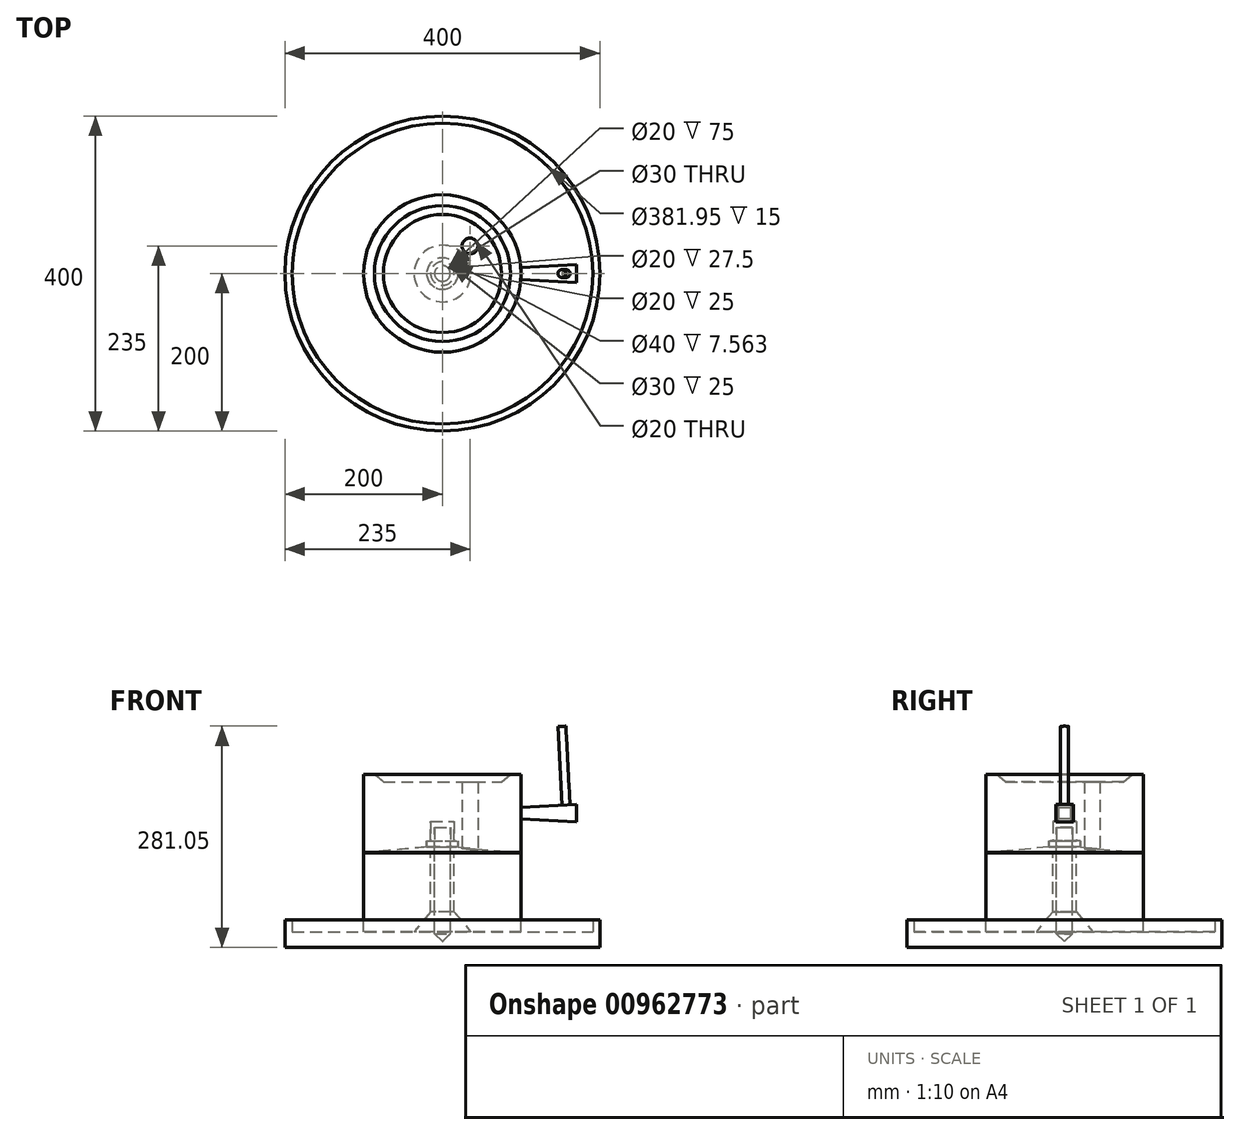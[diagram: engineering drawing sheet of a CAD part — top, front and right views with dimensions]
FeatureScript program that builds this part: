
annotation { "Feature Type Name" : "Feature", "Feature Type Description" : "" }
export const myFeature = defineFeature(function(context is Context, id is Id, definition is map)
    precondition{}
    {
        {
            var Q0;
            Q0=qCreatedBy(makeId("Top.planeOp"),FACE);
            var sketch = newSketch(context, id + "F0", { "sketchPlane" : qUnion([Q0])});
            skCircle(sketch, "E0", {"center": v(0, 0) * mm, "radius": 100 * mm});
            skCircle(sketch, "E1", {"center": v(35, 35) * mm, "radius": 10 * mm});
            skSolve(sketch);
        }
        {
            var Q0;
            Q0=qSketchRegion(id+"F0",true);
            extrude(context, id + "F1", {"entities" : qUnion([Q0]), "depth" : 100 * mm, "offsetDistance" : 25 * mm});
        }
        {
            var Q0;
            Q0=qCreatedBy(makeId("Front.planeOp"),FACE);
            var sketch = newSketch(context, id + "F2", { "sketchPlane" : qUnion([Q0])});
            skLineSegment(sketch, "E2", {"start": v(0, 40) * mm, "end": v(15, 40) * mm});
            skLineSegment(sketch, "E3", {"start": v(0, 0) * mm, "end": v(0, 40) * mm});
            skLineSegment(sketch, "E4", {"start": v(15, 40) * mm, "end": v(15, 15) * mm});
            skLineSegment(sketch, "E5", {"start": v(15, 15) * mm, "end": v(20, 15) * mm});
            skLineSegment(sketch, "E6", {"start": v(20, 15) * mm, "end": v(20, 0) * mm});
            skLineSegment(sketch, "E7", {"start": v(0, 0) * mm, "end": v(20, 0) * mm});
            skSolve(sketch);
        }
        {
            var Q0;
            Q0=qSketchRegion(id+"F2",true);
            var Q1;
            Q1=sQuery(id+"F2.wireOp",EDGE,"E3");
            revolve(context, id + "F3", {"operationType" : NewBodyOperationType.REMOVE, "surfaceOperationType" : NewSurfaceOperationType.NEW, "entities" : qUnion([Q0]), "axis" : qUnion([Q1]), "revolveType" : RevolveType.FULL, "oppositeDirection" : true});
        }
        {
            var Q0;
            Q0=qCreatedBy(makeId("Front.planeOp"),FACE);
            var sketch = newSketch(context, id + "F4", { "sketchPlane" : qUnion([Q0])});
            skLineSegment(sketch, "E8", {"start": v(0, 9.19) * mm, "end": v(105, 0) * mm});
            skLineSegment(sketch, "E9", {"start": v(105, 0) * mm, "end": v(0, 0) * mm});
            skLineSegment(sketch, "E10", {"start": v(0, 0) * mm, "end": v(0, 9.19) * mm});
            skSolve(sketch);
        }
        {
            var Q0;
            Q0=qSketchRegion(id+"F4",true);
            var Q1;
            Q1=sQuery(id+"F4.wireOp",EDGE,"E10");
            revolve(context, id + "F5", {"operationType" : NewBodyOperationType.REMOVE, "surfaceOperationType" : NewSurfaceOperationType.NEW, "entities" : qUnion([Q0]), "axis" : qUnion([Q1]), "revolveType" : RevolveType.FULL, "oppositeDirection" : true});
        }
        {
            var Q0;
            Q0=qCreatedBy(makeId("Top.planeOp"),FACE);
            var sketch = newSketch(context, id + "F6", { "sketchPlane" : qUnion([Q0])});
            skCircle(sketch, "E11", {"center": v(0, 0) * mm, "radius": 100 * mm});
            skSolve(sketch);
        }
        {
            var Q0;
            Q0=qSketchRegion(id+"F6",true);
            extrude(context, id + "F7", {"entities" : qUnion([Q0]), "oppositeDirection" : true, "depth" : 100 * mm, "offsetDistance" : 25 * mm});
        }
        {
            var Q0;
            Q0=qCreatedBy(makeId("Front.planeOp"),FACE);
            var sketch = newSketch(context, id + "F8", { "sketchPlane" : qUnion([Q0])});
            skLineSegment(sketch, "E12", {"start": v(0, 0) * mm, "end": v(15, 0) * mm});
            skLineSegment(sketch, "E13", {"start": v(15, 0) * mm, "end": v(15, -75) * mm});
            skLineSegment(sketch, "E14", {"start": v(15, -75) * mm, "end": v(35.98, -100) * mm});
            skLineSegment(sketch, "E15", {"start": v(35.98, -100) * mm, "end": v(0, -100) * mm});
            skLineSegment(sketch, "E16", {"start": v(0, -100) * mm, "end": v(0, 0) * mm});
            skSolve(sketch);
        }
        {
            var Q0;
            Q0=qSketchRegion(id+"F8",true);
            var Q1;
            Q1=sQuery(id+"F8.wireOp",EDGE,"E16");
            revolve(context, id + "F9", {"operationType" : NewBodyOperationType.REMOVE, "surfaceOperationType" : NewSurfaceOperationType.NEW, "entities" : qUnion([Q0]), "axis" : qUnion([Q1]), "revolveType" : RevolveType.FULL, "oppositeDirection" : true});
        }
        {
            var Q0;
            Q0=qCreatedBy(makeId("Front.planeOp"),FACE);
            var sketch = newSketch(context, id + "F10", { "sketchPlane" : qUnion([Q0])});
            skLineSegment(sketch, "E17", {"start": v(0, 90.44) * mm, "end": v(75, 90.44) * mm});
            skLineSegment(sketch, "E18", {"start": v(75, 90.44) * mm, "end": v(86.4, 100) * mm});
            skLineSegment(sketch, "E19", {"start": v(86.4, 100) * mm, "end": v(0, 100) * mm});
            skLineSegment(sketch, "E20", {"start": v(0, 100) * mm, "end": v(0, 90.44) * mm});
            skSolve(sketch);
        }
        {
            var Q0;
            Q0=qSketchRegion(id+"F10",true);
            var Q1;
            Q1=sQuery(id+"F10.wireOp",EDGE,"E20");
            revolve(context, id + "F11", {"operationType" : NewBodyOperationType.REMOVE, "surfaceOperationType" : NewSurfaceOperationType.NEW, "entities" : qUnion([Q0]), "axis" : qUnion([Q1]), "revolveType" : RevolveType.FULL, "oppositeDirection" : true});
        }
        {
            var Q0;
            Q0=qCreatedBy(makeId("Right.planeOp"),FACE);
            cPlane(context, id + "F12", {"entities" : qUnion([Q0]), "cplaneType" : CPlaneType.OFFSET, "offset" : 100 * mm, "width" : 150 * mm, "height" : 150 * mm});
        }
        {
            var Q0;
            Q0=qCreatedBy(id+"F12.planeOp",FACE);
            var sketch = newSketch(context, id + "F13", { "sketchPlane" : qUnion([Q0])});
            skLineSegment(sketch, "E21.bottom", {"start": v(-7.5, 42.94) * mm, "end": v(7.5, 42.94) * mm});
            skLineSegment(sketch, "E21.top", {"start": v(-7.5, 57.94) * mm, "end": v(7.5, 57.94) * mm});
            skLineSegment(sketch, "E21.left", {"start": v(-7.5, 42.94) * mm, "end": v(-7.5, 57.94) * mm});
            skLineSegment(sketch, "E21.right", {"start": v(7.5, 42.94) * mm, "end": v(7.5, 57.94) * mm});
            skPoint(sketch, "E21.middle", {"position": v(0, 50.44) * mm});
            skSolve(sketch);
        }
        {
            var Q0;
            Q0=qSketchRegion(id+"F13",true);
            extrude(context, id + "F14", {"entities" : qUnion([Q0]), "operationType" : NewBodyOperationType.REMOVE, "oppositeDirection" : true, "depth" : 30 * mm, "offsetDistance" : 25 * mm, "hasDraft" : true, "draftAngle" : 10 * degree, "draftPullDirection" : true});
        }
        {
            var Q0;
            Q0=makeQuery(id+"F14.boolean.opBoolean","COPY",FACE,{"derivedFrom":makeQuery(id+"F14.opExtrude","CAP_FACE",FACE,{"disambiguationData":[OSD([sQuery(id+"F13.wireOp",EDGE,"E21.bottom"),sQuery(id+"F13.wireOp",EDGE,"E21.top"),sQuery(id+"F13.wireOp",EDGE,"E21.left"),sQuery(id+"F13.wireOp",EDGE,"E21.right")])],"isStart":false})});
            extrude(context, id + "F15", {"entities" : qUnion([Q0]), "depth" : 30 * mm, "offsetDistance" : 25 * mm, "hasDraft" : true, "draftAngle" : 10 * degree});
        }
        {
            var Q0;
            Q0=makeQuery(id+"F13.imprint","IMPRINT",FACE,{"disambiguationData":[TD([[makeQuery(id+"F13.imprint","IMPRINT",EDGE,{"derivedFrom":sQuery(id+"F13.wireOp",EDGE,"E21.bottom")}),1.0]])]});
            extrude(context, id + "F16", {"entities" : qUnion([Q0]), "operationType" : NewBodyOperationType.ADD, "depth" : 70 * mm, "offsetDistance" : 25 * mm, "hasDraft" : true, "draftAngle" : 3 * degree});
        }
        {
            var Q0;
            Q0=makeQuery(id+"F16.opExtrude","SWEPT_FACE",FACE,{"disambiguationData":[OSD([sQuery(id+"F13.wireOp",EDGE,"E21.top")])]});
            var sketch = newSketch(context, id + "F17", { "sketchPlane" : qUnion([Q0])});
            skCircle(sketch, "E22", {"center": v(160, 0) * mm, "radius": 5 * mm});
            skSolve(sketch);
        }
        {
            var Q0;
            Q0=qSketchRegion(id+"F17",true);
            extrude(context, id + "F18", {"entities" : qUnion([Q0]), "operationType" : NewBodyOperationType.ADD, "depth" : 100 * mm, "offsetDistance" : 25 * mm});
        }
        {
            var Q0;
            Q0=qCreatedBy(makeId("Front.planeOp"),FACE);
            var sketch = newSketch(context, id + "F19", { "sketchPlane" : qUnion([Q0])});
            skLineSegment(sketch, "E23", {"start": v(0, 40) * mm, "end": v(15, 40) * mm});
            skLineSegment(sketch, "E24", {"start": v(15, 40) * mm, "end": v(15, 15) * mm});
            skLineSegment(sketch, "E25", {"start": v(15, 15) * mm, "end": v(20, 15) * mm});
            skLineSegment(sketch, "E26", {"start": v(20, 15) * mm, "end": v(20, 7.5) * mm});
            skLineSegment(sketch, "E27", {"start": v(20, 7.5) * mm, "end": v(0, 7.5) * mm});
            skLineSegment(sketch, "E28", {"start": v(0, 7.5) * mm, "end": v(0, 40) * mm});
            skSolve(sketch);
        }
        {
            var Q0;
            Q0=qSketchRegion(id+"F19",true);
            var Q1;
            Q1=sQuery(id+"F2.wireOp",EDGE,"E3");
            revolve(context, id + "F20", {"surfaceOperationType" : NewSurfaceOperationType.NEW, "entities" : qUnion([Q0]), "axis" : qUnion([Q1]), "revolveType" : RevolveType.FULL});
        }
        {
            var Q0;
            Q0=makeQuery(id+"F20.opRevolve","SWEPT_FACE",FACE,{"disambiguationData":[OSD([sQuery(id+"F19.wireOp",EDGE,"E27")])]});
            var sketch = newSketch(context, id + "F21", { "sketchPlane" : qUnion([Q0])});
            skCircle(sketch, "E29", {"center": v(0, 0) * mm, "radius": 10 * mm});
            skSolve(sketch);
        }
        {
            var Q0;
            Q0=qSketchRegion(id+"F21",true);
            extrude(context, id + "F22", {"entities" : qUnion([Q0]), "operationType" : NewBodyOperationType.REMOVE, "oppositeDirection" : true, "depth" : 25 * mm, "offsetDistance" : 25 * mm});
        }
        {
            var Q0;
            Q0=qCreatedBy(makeId("Top.planeOp"),FACE);
            var sketch = newSketch(context, id + "F23", { "sketchPlane" : qUnion([Q0])});
            skCircle(sketch, "E30.0", {"center": v(0, 0) * mm, "radius": 15 * mm});
            skSolve(sketch);
        }
        {
            var Q0;
            Q0=qSketchRegion(id+"F23",true);
            extrude(context, id + "F24", {"entities" : qUnion([Q0]), "oppositeDirection" : true, "depth" : 75 * mm, "offsetDistance" : 25 * mm});
        }
        {
            var Q0;
            Q0=makeQuery(id+"F24.opExtrude","CAP_FACE",FACE,{"disambiguationData":[OSD([sQuery(id+"F23.wireOp",EDGE,"E30.0")])],"isStart":true});
            var sketch = newSketch(context, id + "F25", { "sketchPlane" : qUnion([Q0])});
            skCircle(sketch, "E31", {"center": v(0, 0) * mm, "radius": 10 * mm});
            skSolve(sketch);
        }
        {
            var Q0;
            Q0=qSketchRegion(id+"F25",true);
            extrude(context, id + "F26", {"entities" : qUnion([Q0]), "operationType" : NewBodyOperationType.REMOVE, "oppositeDirection" : true, "depth" : 75 * mm, "offsetDistance" : 25 * mm});
        }
        {
            var Q0;
            Q0=makeQuery(id+"F22.boolean.opBoolean","COPY",FACE,{"derivedFrom":makeQuery(id+"F22.opExtrude","CAP_FACE",FACE,{"disambiguationData":[OSD([sQuery(id+"F21.wireOp",EDGE,"E29")])],"isStart":false})});
            var sketch = newSketch(context, id + "F27", { "sketchPlane" : qUnion([Q0])});
            skCircle(sketch, "E32.0.0", {"center": v(0, 0) * mm, "radius": 10 * mm});
            skSolve(sketch);
        }
        {
            var Q0;
            Q0=qSketchRegion(id+"F27",true);
            extrude(context, id + "F28", {"entities" : qUnion([Q0]), "depth" : 145 * mm, "offsetDistance" : 25 * mm});
        }
        {
            var Q0;
            Q0=makeQuery(id+"F28.opExtrude","CAP_EDGE",EDGE,{"disambiguationData":[OSD([sQuery(id+"F27.wireOp",EDGE,"E32.0.0")])],"isStart":false});
            chamfer(context, id + "F29", {"entities" : qUnion([Q0]), "width" : 10 * mm, "tangentPropagation" : true});
        }
        {
            var Q0;
            Q0=qCreatedBy(makeId("Front.planeOp"),FACE);
            var sketch = newSketch(context, id + "F30", { "sketchPlane" : qUnion([Q0])});
            skLineSegment(sketch, "E33", {"start": v(190.98, -100) * mm, "end": v(190.98, -85) * mm});
            skLineSegment(sketch, "E34", {"start": v(190.98, -85) * mm, "end": v(200, -85) * mm});
            skLineSegment(sketch, "E35", {"start": v(200, -85) * mm, "end": v(200, -120) * mm});
            skLineSegment(sketch, "E36", {"start": v(200, -120) * mm, "end": v(0, -120) * mm});
            skLineSegment(sketch, "E37", {"start": v(0, -120) * mm, "end": v(0, -75) * mm});
            skLineSegment(sketch, "E38", {"start": v(0, -75) * mm, "end": v(15, -75) * mm});
            skLineSegment(sketch, "E39", {"start": v(15, -75) * mm, "end": v(35.98, -100) * mm});
            skLineSegment(sketch, "E40", {"start": v(35.98, -100) * mm, "end": v(190.98, -100) * mm});
            skSolve(sketch);
        }
        {
            var Q0;
            Q0=qSketchRegion(id+"F30",true);
            var Q1;
            Q1=sQuery(id+"F30.wireOp",EDGE,"E37");
            revolve(context, id + "F31", {"surfaceOperationType" : NewSurfaceOperationType.NEW, "entities" : qUnion([Q0]), "axis" : qUnion([Q1]), "revolveType" : RevolveType.FULL});
        }
        {
            var Q0;
            Q0=makeQuery(id+"F28.opExtrude","SWEPT_BODY",BODY,{"disambiguationData":[OSD([sQuery(id+"F27.wireOp",EDGE,"E32.0.0")])]});
            var Q1;
            Q1=makeQuery(id+"F31.opRevolve","SWEPT_BODY",BODY,{"disambiguationData":[OSD([sQuery(id+"F30.wireOp",EDGE,"x0PHMXUQ-w0mN-wSCU-o6u4-OQjVglI4lZyS"),sQuery(id+"F30.wireOp",EDGE,"E33"),sQuery(id+"F30.wireOp",EDGE,"E34"),sQuery(id+"F30.wireOp",EDGE,"E35"),sQuery(id+"F30.wireOp",EDGE,"E36"),sQuery(id+"F30.wireOp",EDGE,"h7mgvtze-5PXb-mjpW-W06Y-tg9THzuJcQCp")])]});
            booleanBodies(context, id + "F32", {"operationType" : BooleanOperationType.SUBTRACTION, "tools" : qUnion([Q0]), "targets" : qUnion([Q1]), "keepTools" : true});
        }
    });
